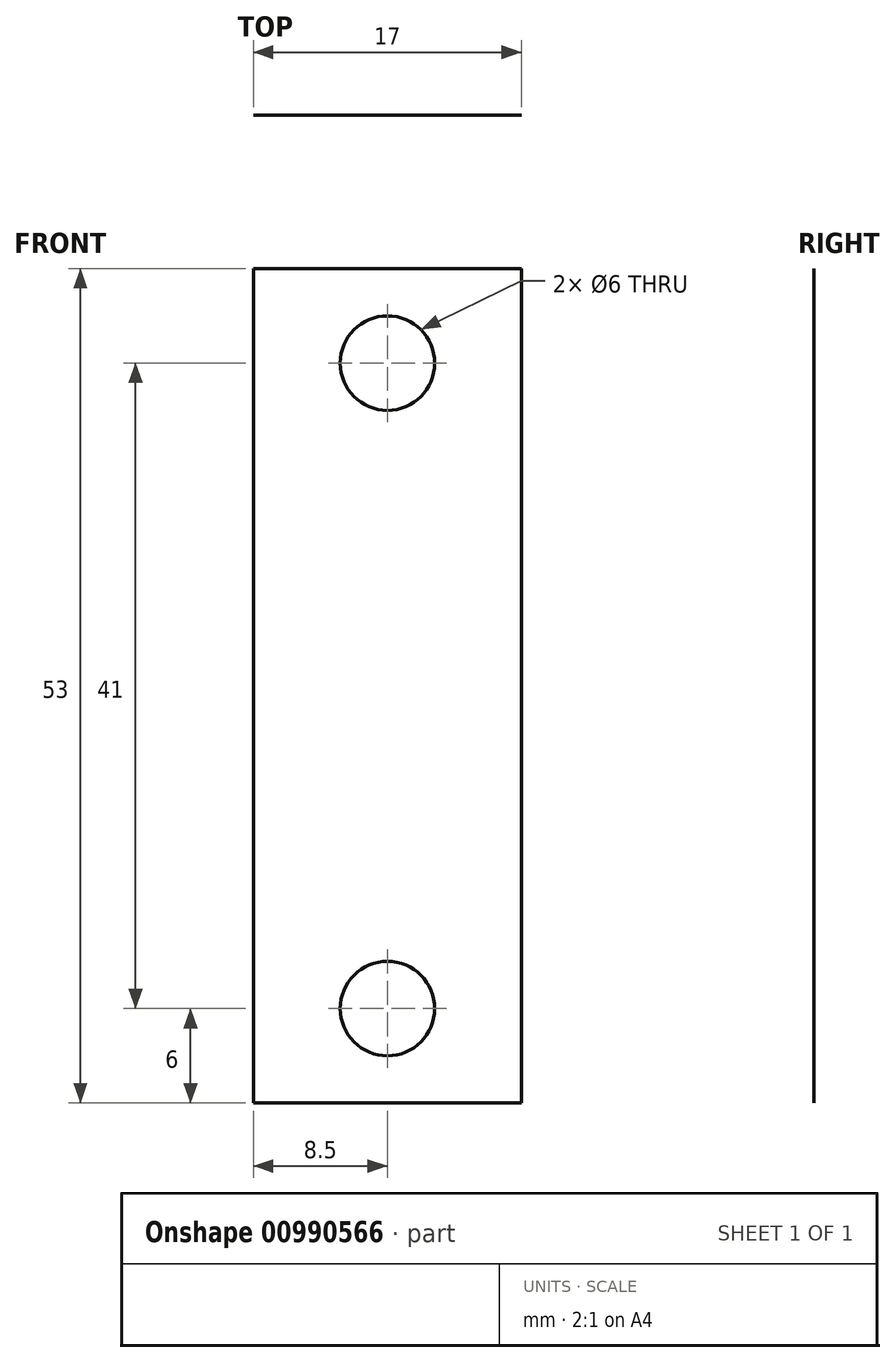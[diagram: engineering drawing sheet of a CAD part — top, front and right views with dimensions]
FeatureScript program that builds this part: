
annotation { "Feature Type Name" : "Feature", "Feature Type Description" : "" }
export const myFeature = defineFeature(function(context is Context, id is Id, definition is map)
    precondition{}
    {
        {
            var Q0;
            Q0=qCreatedBy(makeId("Front.planeOp"),FACE);
            var sketch = newSketch(context, id + "F0", { "sketchPlane" : qUnion([Q0])});
            skLineSegment(sketch, "E0.bottom", {"start": v(8.5, 26.5) * mm, "end": v(-8.5, 26.5) * mm});
            skLineSegment(sketch, "E0.top", {"start": v(8.5, -26.5) * mm, "end": v(-8.5, -26.5) * mm});
            skLineSegment(sketch, "E0.left", {"start": v(8.5, 26.5) * mm, "end": v(8.5, -26.5) * mm});
            skLineSegment(sketch, "E0.right", {"start": v(-8.5, 26.5) * mm, "end": v(-8.5, -26.5) * mm});
            skPoint(sketch, "E0.middle", {"position": v(0, 0) * mm});
            skCircle(sketch, "E1", {"center": v(0, 20.5) * mm, "radius": 3 * mm});
            skCircle(sketch, "E2", {"center": v(0, -20.5) * mm, "radius": 3 * mm});
            skSolve(sketch);
        }
        {
            var Q0;
            Q0 = qSketchRegion(id + "F0", true);
            extrude(context, id + "F1", {"entities" : qUnion([Q0]), "depth" : 1 / 203.2 * mm, "offsetDistance" : 25.4 * mm});
        }
    });
